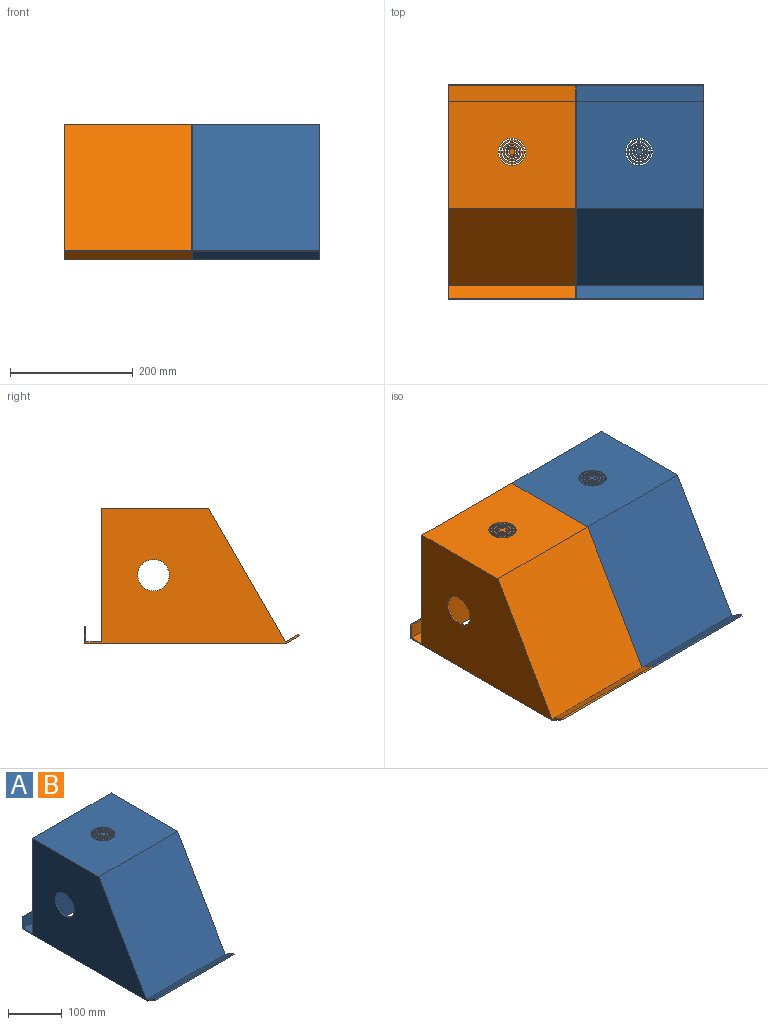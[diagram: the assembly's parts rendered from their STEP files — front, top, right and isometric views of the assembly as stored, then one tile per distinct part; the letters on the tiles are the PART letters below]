
ASSEMBLY  parts=2 mates=1
PART A: 84 faces, bbox 207.5x351.2x220 mm
  f0: plane 207.5x25mm, normal (0,0,1), area 5187.5mm2, adj f1,f5,f7,f82
  f1: plane 217.5x207.5mm, normal (0,1,0), area 45131.2mm2, adj f0,f2,f5,f7
  f2: plane 207.5x175mm, normal (0,0,1), area 35555.9mm2, adj f1,f5,f6,f7,f12,f13,f14,f15
  f3: plane 202.5x171.06mm, normal (0,0,-1), area 33882.4mm2, adj f8,f9,f10,f11,f12,f13,f14,f15
  f4: plane 329.52x207.5mm, normal (0,0,-1), area 8307.2mm2, adj f5,f7,f8,f9,f10,f11,f76,f78
  f5: plane 351.17x220mm, normal (-1,0,0), area 50596.6mm2, adj f0,f1,f2,f4,f6,f76,f77,f78
  f6: plane 217.5x207.5mm, normal (0,-0.87,0.5), area 52113.1mm2, adj f2,f5,f7,f77
  f7: plane 351.17x220mm, normal (1,0,0), area 50596.6mm2, adj f0,f1,f2,f4,f6,f76,f77,f78
  f8: plane 217.5x202.5mm, normal (0,-1,0), area 44043.8mm2, adj f3,f4,f9,f11
  f9: plane 296.63x217.5mm, normal (1,0,0), area 48782.3mm2, adj f3,f4,f8,f10,f81
  f10: plane 217.5x202.5mm, normal (0,0.87,-0.5), area 50857.3mm2, adj f3,f4,f9,f11
  f11: plane 296.63x217.5mm, normal (-1,0,0), area 48782.3mm2, adj f3,f4,f8,f10,f80
  f12: plane 2.5x2.5mm, normal (-1,0,0), area 6.3mm2, adj f2,f3,f13,f15
  f13: cylinder r=22.39mm len=21.1mm, axis (0,0,1), area 81.7mm2, adj f2,f3,f12,f14
  f14: plane 2.5x2.5mm, normal (0,1,0), area 6.3mm2, adj f2,f3,f13,f15
  f15: cylinder r=19.89mm len=18.6mm, axis (0,0,1), area 71.8mm2, adj f2,f3,f12,f14
  f16: cylinder r=7.39mm len=6.03mm, axis (0,0,1), area 22.7mm2, adj f2,f3,f17,f19
  f17: plane 2.56x2.5mm, normal (1,0,0), area 6.4mm2, adj f2,f3,f16,f18
  f18: cylinder r=4.89mm len=3.48mm, axis (0,0,1), area 12.9mm2, adj f2,f3,f17,f19
  f19: plane 2.56x2.5mm, normal (0,1,0), area 6.4mm2, adj f2,f3,f16,f18
  f20: cylinder r=19.89mm len=18.6mm, axis (0,0,1), area 71.8mm2, adj f2,f3,f21,f23
  f21: plane 2.5x2.5mm, normal (1,0,0), area 6.3mm2, adj f2,f3,f20,f22
  f22: cylinder r=22.39mm len=21.1mm, axis (0,0,1), area 81.7mm2, adj f2,f3,f21,f23
  f23: plane 2.5x2.5mm, normal (0,-1,0), area 6.3mm2, adj f2,f3,f20,f22
  f24: cylinder r=9.89mm len=8.56mm, axis (0,0,1), area 32.6mm2, adj f2,f3,f25,f27
  f25: plane 2.52x2.5mm, normal (1,0,0), area 6.3mm2, adj f2,f3,f24,f26
  f26: cylinder r=12.39mm len=11.07mm, axis (0,0,1), area 42.4mm2, adj f2,f3,f25,f27
  f27: plane 2.52x2.5mm, normal (0,-1,0), area 6.3mm2, adj f2,f3,f24,f26
  f28: cylinder r=14.89mm len=13.59mm, axis (0,0,1), area 52.2mm2, adj f2,f3,f29,f31
  f29: plane 2.51x2.5mm, normal (1,0,0), area 6.3mm2, adj f2,f3,f28,f30
  f30: cylinder r=17.39mm len=16.09mm, axis (0,0,1), area 62mm2, adj f2,f3,f29,f31
  f31: plane 2.51x2.5mm, normal (0,-1,0), area 6.3mm2, adj f2,f3,f28,f30
  f32: plane 2.5x2.5mm, normal (0,1,0), area 6.3mm2, adj f2,f3,f33,f35
  f33: cylinder r=22.39mm len=21.1mm, axis (0,0,1), area 81.7mm2, adj f2,f3,f32,f34
  f34: plane 2.5x2.5mm, normal (1,0,0), area 6.3mm2, adj f2,f3,f33,f35
  f35: cylinder r=19.89mm len=18.6mm, axis (0,0,1), area 71.8mm2, adj f2,f3,f32,f34
  f36: cylinder r=12.39mm len=11.07mm, axis (0,0,1), area 42.4mm2, adj f2,f3,f37,f39
  f37: plane 2.52x2.5mm, normal (1,0,0), area 6.3mm2, adj f2,f3,f36,f38
  f38: cylinder r=9.89mm len=8.56mm, axis (0,0,1), area 32.6mm2, adj f2,f3,f37,f39
  f39: plane 2.52x2.5mm, normal (0,1,0), area 6.3mm2, adj f2,f3,f36,f38
  f40: cylinder r=17.39mm len=16.09mm, axis (0,0,1), area 62mm2, adj f2,f3,f41,f43
  f41: plane 2.51x2.5mm, normal (1,0,0), area 6.3mm2, adj f2,f3,f40,f42
  f42: cylinder r=14.89mm len=13.59mm, axis (0,0,1), area 52.2mm2, adj f2,f3,f41,f43
  f43: plane 2.51x2.5mm, normal (0,1,0), area 6.3mm2, adj f2,f3,f40,f42
  f44: plane 2.5x2.5mm, normal (-1,0,0), area 6.3mm2, adj f2,f3,f45,f47
  f45: cylinder r=19.89mm len=18.6mm, axis (0,0,1), area 71.8mm2, adj f2,f3,f44,f46
  f46: plane 2.5x2.5mm, normal (0,-1,0), area 6.3mm2, adj f2,f3,f45,f47
  f47: cylinder r=22.39mm len=21.1mm, axis (0,0,1), area 81.7mm2, adj f2,f3,f44,f46
  f48: plane 2.56x2.5mm, normal (-1,0,0), area 6.4mm2, adj f2,f3,f49,f51
  f49: cylinder r=7.39mm len=6.03mm, axis (0,0,1), area 22.7mm2, adj f2,f3,f48,f50
  f50: plane 2.56x2.5mm, normal (0,1,0), area 6.4mm2, adj f2,f3,f49,f51
  f51: cylinder r=4.89mm len=3.48mm, axis (0,0,1), area 12.9mm2, adj f2,f3,f48,f50
  f52: plane 2.51x2.5mm, normal (-1,0,0), area 6.3mm2, adj f2,f3,f53,f55
  f53: cylinder r=17.39mm len=16.09mm, axis (0,0,1), area 62mm2, adj f2,f3,f52,f54
  f54: plane 2.51x2.5mm, normal (0,1,0), area 6.3mm2, adj f2,f3,f53,f55
  f55: cylinder r=14.89mm len=13.59mm, axis (0,0,1), area 52.2mm2, adj f2,f3,f52,f54
  f56: plane 2.52x2.5mm, normal (-1,0,0), area 6.3mm2, adj f2,f3,f57,f59
  f57: cylinder r=12.39mm len=11.07mm, axis (0,0,1), area 42.4mm2, adj f2,f3,f56,f58
  f58: plane 2.52x2.5mm, normal (0,1,0), area 6.3mm2, adj f2,f3,f57,f59
  f59: cylinder r=9.89mm len=8.56mm, axis (0,0,1), area 32.6mm2, adj f2,f3,f56,f58
  f60: cylinder r=4.89mm len=3.48mm, axis (0,0,1), area 12.9mm2, adj f2,f3,f61,f63
  f61: plane 2.56x2.5mm, normal (1,0,0), area 6.4mm2, adj f2,f3,f60,f62
  f62: cylinder r=7.39mm len=6.03mm, axis (0,0,1), area 22.7mm2, adj f2,f3,f61,f63
  f63: plane 2.56x2.5mm, normal (0,-1,0), area 6.4mm2, adj f2,f3,f60,f62
  f64: plane 2.56x2.5mm, normal (-1,0,0), area 6.4mm2, adj f2,f3,f65,f67
  f65: cylinder r=4.89mm len=3.48mm, axis (0,0,1), area 12.9mm2, adj f2,f3,f64,f66
  f66: plane 2.56x2.5mm, normal (0,-1,0), area 6.4mm2, adj f2,f3,f65,f67
  f67: cylinder r=7.39mm len=6.03mm, axis (0,0,1), area 22.7mm2, adj f2,f3,f64,f66
  f68: plane 2.51x2.5mm, normal (-1,0,0), area 6.3mm2, adj f2,f3,f69,f71
  f69: cylinder r=14.89mm len=13.59mm, axis (0,0,1), area 52.2mm2, adj f2,f3,f68,f70
  f70: plane 2.51x2.5mm, normal (0,-1,0), area 6.3mm2, adj f2,f3,f69,f71
  f71: cylinder r=17.39mm len=16.09mm, axis (0,0,1), area 62mm2, adj f2,f3,f68,f70
  f72: plane 2.52x2.5mm, normal (-1,0,0), area 6.3mm2, adj f2,f3,f73,f75
  f73: cylinder r=9.89mm len=8.56mm, axis (0,0,1), area 32.6mm2, adj f2,f3,f72,f74
  f74: plane 2.52x2.5mm, normal (0,-1,0), area 6.3mm2, adj f2,f3,f73,f75
  f75: cylinder r=12.39mm len=11.07mm, axis (0,0,1), area 42.4mm2, adj f2,f3,f72,f74
  f76: plane 207.5x27.5mm, normal (0,1,0), area 5706.2mm2, adj f4,f5,f7,f83
  f77: plane 207.5x21.65mm, normal (0,0.5,0.87), area 5187.5mm2, adj f5,f6,f7,f79
  f78: plane 207.5x21.65mm, normal (0,-0.5,-0.87), area 5187.5mm2, adj f4,f5,f7,f79
  f79: plane 207.5x2.5mm, normal (0,-0.87,0.5), area 599mm2, adj f5,f7,f77,f78
  f80: cylinder r=25.72mm len=51.45mm, axis (1,0,0), area 404.1mm2, adj f7,f11
  f81: cylinder r=25.72mm len=51.45mm, axis (1,0,0), area 404.1mm2, adj f5,f9
  f82: plane 207.5x25mm, normal (0,-1,0), area 5187.5mm2, adj f0,f5,f7,f83
  f83: plane 207.5x2.5mm, normal (0,0,1), area 518.8mm2, adj f5,f7,f76,f82
PART B: same geometry as A
PLACE A t=(418.12,174.92,-91.82)mm
PLACE B t=(210.62,174.92,-91.82)mm
MATE parallel B.f7 <-> A.f5  axis (1,0,0) through (315.01,134.22,7.59)mm
